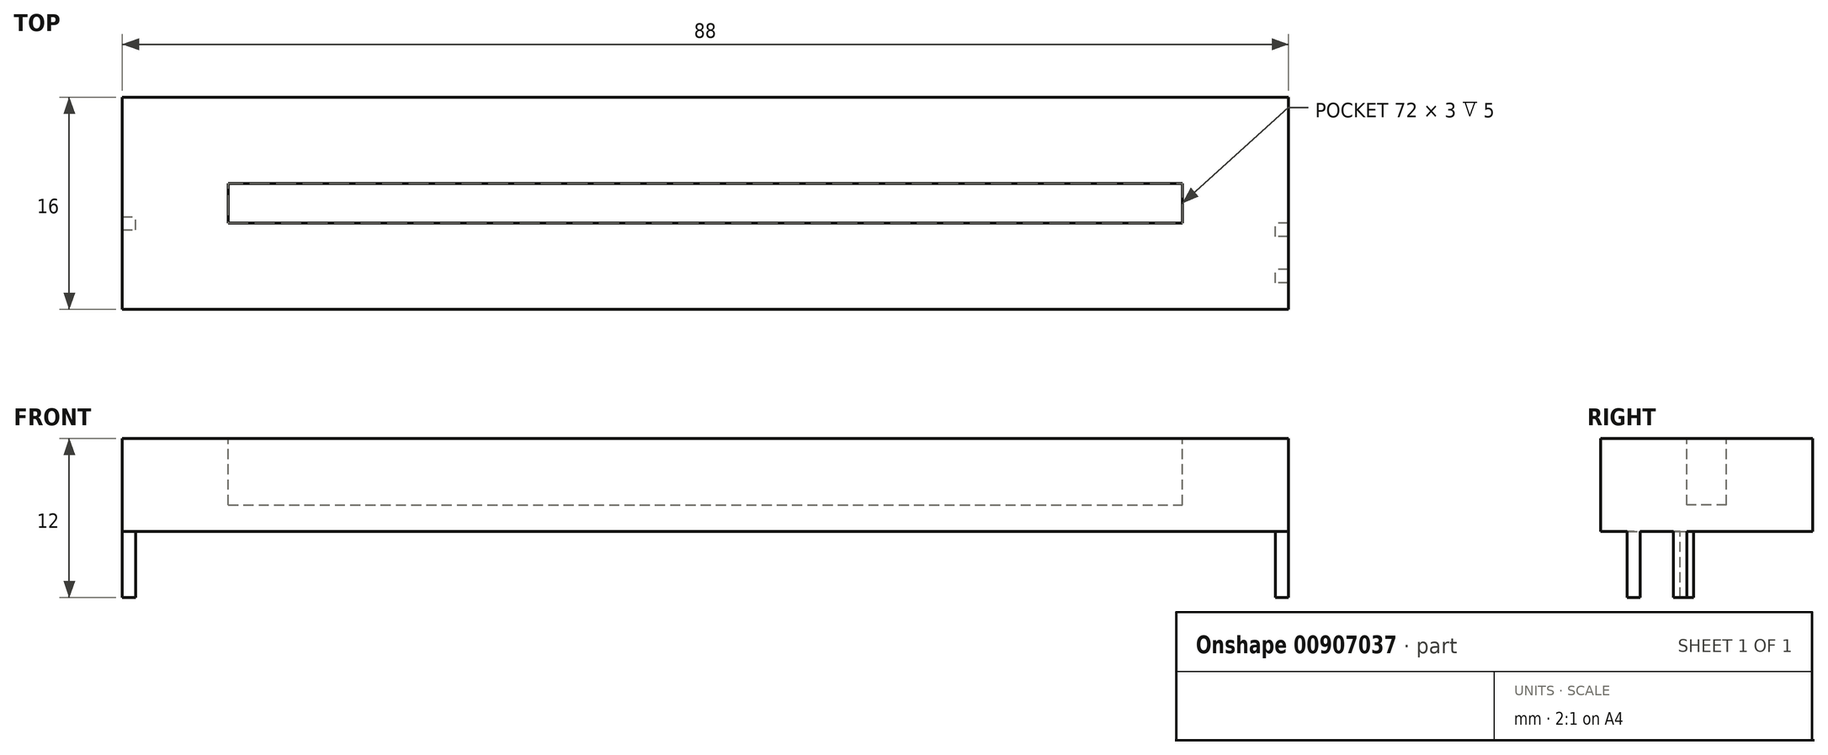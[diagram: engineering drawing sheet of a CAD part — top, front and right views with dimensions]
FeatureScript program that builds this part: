
annotation { "Feature Type Name" : "Feature", "Feature Type Description" : "" }
export const myFeature = defineFeature(function(context is Context, id is Id, definition is map)
    precondition{}
    {
        {
            var Q0;
            Q0=qCreatedBy(makeId("Top.planeOp"),FACE);
            var sketch = newSketch(context, id + "F0", { "sketchPlane" : qUnion([Q0])});
            skLineSegment(sketch, "E0.bottom", {"start": v(-44, 8) * mm, "end": v(44, 8) * mm});
            skLineSegment(sketch, "E0.top", {"start": v(-44, -8) * mm, "end": v(44, -8) * mm});
            skLineSegment(sketch, "E0.left", {"start": v(-44, 8) * mm, "end": v(-44, -8) * mm});
            skLineSegment(sketch, "E0.right", {"start": v(44, 8) * mm, "end": v(44, -8) * mm});
            skSolve(sketch);
        }
        {
            var Q0;
            Q0=makeQuery(id+"F0.imprint","IMPRINT",FACE,{"disambiguationData":[TD([[makeQuery(id+"F0.imprint","IMPRINT",EDGE,{"derivedFrom":sQuery(id+"F0.wireOp",EDGE,"E0.bottom")}),-1.0]])]});
            extrude(context, id + "F1", {"entities" : qUnion([Q0]), "depth" : 7 * mm, "offsetDistance" : 25 * mm});
        }
        {
            var Q0;
            Q0=makeQuery(id+"F1.opExtrude","CAP_FACE",FACE,{"disambiguationData":[OSD([sQuery(id+"F0.wireOp",EDGE,"E0.bottom"),sQuery(id+"F0.wireOp",EDGE,"E0.top"),sQuery(id+"F0.wireOp",EDGE,"E0.left"),sQuery(id+"F0.wireOp",EDGE,"E0.right")])],"isStart":false});
            var sketch = newSketch(context, id + "F2", { "sketchPlane" : qUnion([Q0])});
            skLineSegment(sketch, "E1.bottom", {"start": v(-36, 1.5) * mm, "end": v(36, 1.5) * mm});
            skLineSegment(sketch, "E1.top", {"start": v(-36, -1.5) * mm, "end": v(36, -1.5) * mm});
            skLineSegment(sketch, "E1.left", {"start": v(-36, 1.5) * mm, "end": v(-36, -1.5) * mm});
            skLineSegment(sketch, "E1.right", {"start": v(36, 1.5) * mm, "end": v(36, -1.5) * mm});
            skSolve(sketch);
        }
        {
            var Q0;
            Q0=makeQuery(id+"F2.imprint","IMPRINT",FACE,{"disambiguationData":[TD([[makeQuery(id+"F2.imprint","IMPRINT",EDGE,{"derivedFrom":sQuery(id+"F2.wireOp",EDGE,"E1.bottom")}),-1.0]])]});
            extrude(context, id + "F3", {"entities" : qUnion([Q0]), "operationType" : NewBodyOperationType.REMOVE, "oppositeDirection" : true, "depth" : 5 * mm, "offsetDistance" : 25 * mm});
        }
        {
            var Q0;
            Q0=makeQuery(id+"F1.opExtrude","CAP_FACE",FACE,{"disambiguationData":[OSD([sQuery(id+"F0.wireOp",EDGE,"E0.bottom"),sQuery(id+"F0.wireOp",EDGE,"E0.top"),sQuery(id+"F0.wireOp",EDGE,"E0.left"),sQuery(id+"F0.wireOp",EDGE,"E0.right")])],"isStart":true});
            var sketch = newSketch(context, id + "F4", { "sketchPlane" : qUnion([Q0])});
            skLineSegment(sketch, "E2.bottom", {"start": v(-44, 2) * mm, "end": v(-43, 2) * mm});
            skLineSegment(sketch, "E2.top", {"start": v(-44, 1) * mm, "end": v(-43, 1) * mm});
            skLineSegment(sketch, "E2.left", {"start": v(-44, 2) * mm, "end": v(-44, 1) * mm});
            skLineSegment(sketch, "E2.right", {"start": v(-43, 2) * mm, "end": v(-43, 1) * mm});
            skLineSegment(sketch, "E3.bottom", {"start": v(44, 6) * mm, "end": v(43, 6) * mm});
            skLineSegment(sketch, "E3.top", {"start": v(44, 5) * mm, "end": v(43, 5) * mm});
            skLineSegment(sketch, "E3.left", {"start": v(44, 6) * mm, "end": v(44, 5) * mm});
            skLineSegment(sketch, "E3.right", {"start": v(43, 6) * mm, "end": v(43, 5) * mm});
            skLineSegment(sketch, "E4.bottom", {"start": v(44, 2.5) * mm, "end": v(43, 2.5) * mm});
            skLineSegment(sketch, "E4.top", {"start": v(44, 1.5) * mm, "end": v(43, 1.5) * mm});
            skLineSegment(sketch, "E4.left", {"start": v(44, 2.5) * mm, "end": v(44, 1.5) * mm});
            skLineSegment(sketch, "E4.right", {"start": v(43, 2.5) * mm, "end": v(43, 1.5) * mm});
            skSolve(sketch);
        }
        {
            var Q0;
            Q0=makeQuery(id+"F4.imprint","IMPRINT",FACE,{"disambiguationData":[TD([[makeQuery(id+"F4.imprint","IMPRINT",EDGE,{"derivedFrom":sQuery(id+"F4.wireOp",EDGE,"E2.bottom")}),-1.0]])]});
            var Q1;
            Q1=makeQuery(id+"F4.imprint","IMPRINT",FACE,{"disambiguationData":[TD([[makeQuery(id+"F4.imprint","IMPRINT",EDGE,{"derivedFrom":sQuery(id+"F4.wireOp",EDGE,"E3.bottom")}),1.0]])]});
            var Q2;
            Q2=makeQuery(id+"F4.imprint","IMPRINT",FACE,{"disambiguationData":[TD([[makeQuery(id+"F4.imprint","IMPRINT",EDGE,{"derivedFrom":sQuery(id+"F4.wireOp",EDGE,"E4.bottom")}),1.0]])]});
            extrude(context, id + "F5", {"entities" : qUnion([Q0, Q1, Q2]), "operationType" : NewBodyOperationType.ADD, "depth" : 5 * mm, "offsetDistance" : 25 * mm});
        }
    });
